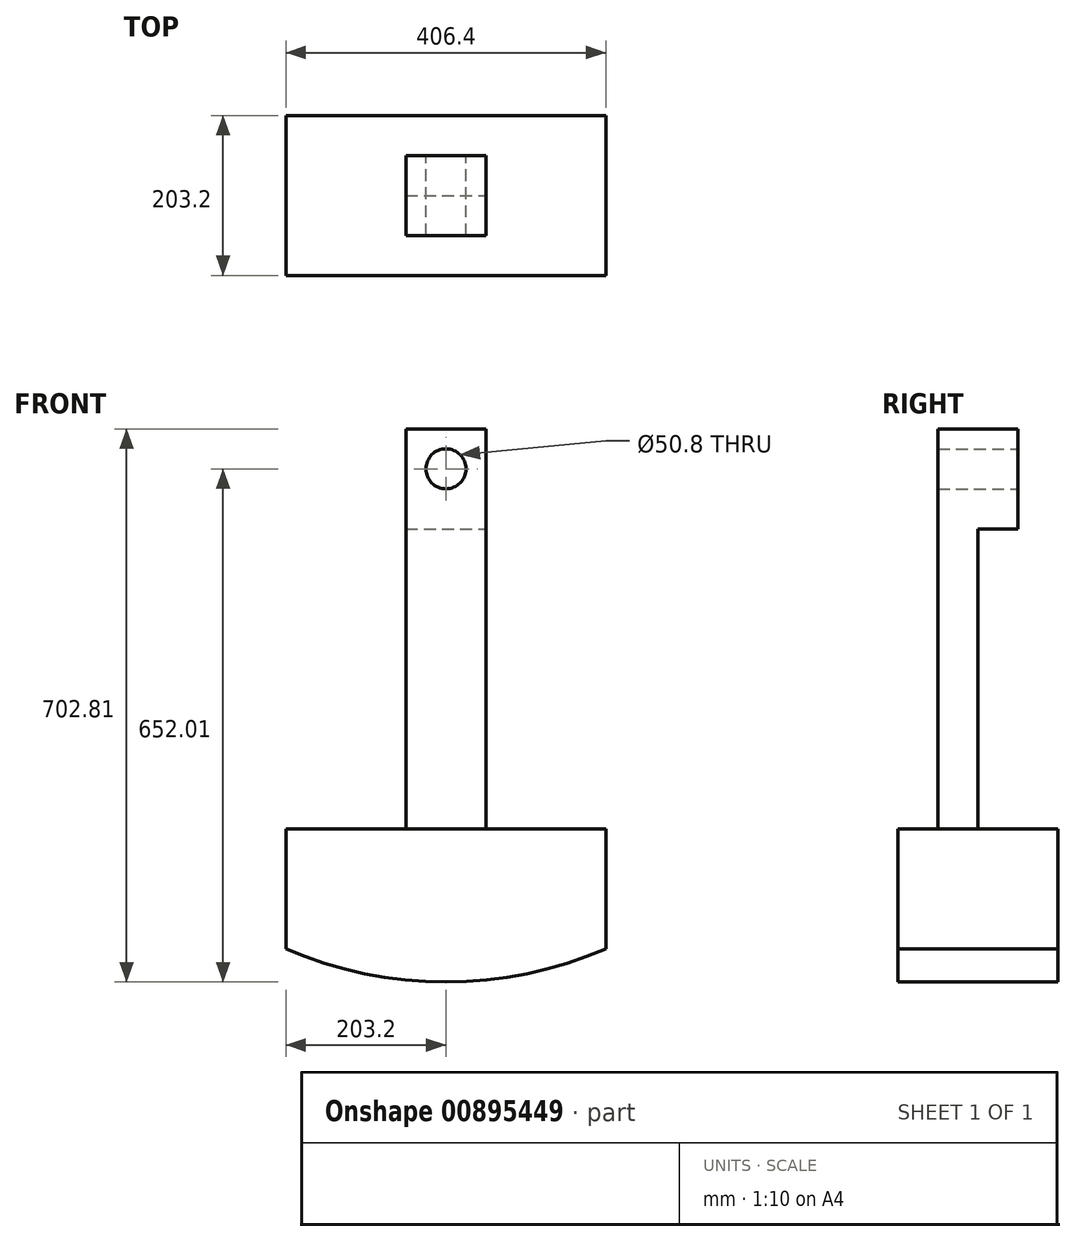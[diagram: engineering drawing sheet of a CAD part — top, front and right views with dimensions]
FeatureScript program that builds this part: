
annotation { "Feature Type Name" : "Feature", "Feature Type Description" : "" }
export const myFeature = defineFeature(function(context is Context, id is Id, definition is map)
    precondition{}
    {
        {
            var Q0;
            Q0=qCreatedBy(makeId("Front.planeOp"),FACE);
            var sketch = newSketch(context, id + "F0", { "sketchPlane" : qUnion([Q0])});
            skLineSegment(sketch, "E0.bottom", {"start": v(-50.8, 0) * mm, "end": v(50.8, 0) * mm});
            skLineSegment(sketch, "E0.top", {"start": v(-50.8, 508) * mm, "end": v(50.8, 508) * mm});
            skLineSegment(sketch, "E0.left", {"start": v(-50.8, 0) * mm, "end": v(-50.8, 508) * mm});
            skLineSegment(sketch, "E0.right", {"start": v(50.8, 0) * mm, "end": v(50.8, 508) * mm});
            skCircle(sketch, "E1", {"center": v(0, 457.2) * mm, "radius": 25.4 * mm});
            skSolve(sketch);
        }
        {
            var Q0;
            Q0=makeQuery(id+"F0.imprint","IMPRINT",FACE,{"disambiguationData":[TD([[makeQuery(id+"F0.imprint","IMPRINT",EDGE,{"derivedFrom":sQuery(id+"F0.wireOp",EDGE,"E0.bottom")}),1.0]])]});
            extrude(context, id + "F1", {"entities" : qUnion([Q0]), "endBound" : BoundingType.SYMMETRIC, "depth" : 101.6 * mm, "offsetDistance" : 25.4 * mm});
        }
        {
            var Q0;
            Q0=qCreatedBy(makeId("Front.planeOp"),FACE);
            var sketch = newSketch(context, id + "F2", { "sketchPlane" : qUnion([Q0])});
            skLineSegment(sketch, "E2", {"start": v(-203.2, 0) * mm, "end": v(203.2, 0) * mm});
            skArc(sketch, "E3", {"start": v(-203.2, -152.4) * mm, "mid": v(0, -194.81) * mm, "end": v(203.2, -152.4) * mm});
            skPoint(sketch, "E3.first.point", {"position": v(0, 821.19) * mm});
            skPoint(sketch, "E3.second.point", {"position": v(0, -194.81) * mm});
            skPoint(sketch, "E3.third.point", {"position": v(254.5, -126.47) * mm});
            skLineSegment(sketch, "E4", {"start": v(-203.2, 0) * mm, "end": v(-203.2, -152.4) * mm});
            skLineSegment(sketch, "E5", {"start": v(203.2, 0) * mm, "end": v(203.2, -152.4) * mm});
            skSolve(sketch);
        }
        {
            var Q0;
            Q0=makeQuery(id+"F2.imprint","IMPRINT",FACE,{"disambiguationData":[TD([[makeQuery(id+"F2.imprint","IMPRINT",EDGE,{"derivedFrom":sQuery(id+"F2.wireOp",EDGE,"E2")}),-1.0]])]});
            extrude(context, id + "F3", {"entities" : qUnion([Q0]), "operationType" : NewBodyOperationType.ADD, "endBound" : BoundingType.SYMMETRIC, "depth" : 203.2 * mm, "offsetDistance" : 25.4 * mm});
        }
        {
            var Q0;
            Q0=makeQuery(id+"F1.opExtrude","SWEPT_FACE",FACE,{"disambiguationData":[OSD([sQuery(id+"F0.wireOp",EDGE,"E0.right")])]});
            var sketch = newSketch(context, id + "F4", { "sketchPlane" : qUnion([Q0])});
            skLineSegment(sketch, "E6.bottom", {"start": v(50.8, 0) * mm, "end": v(0, 0) * mm});
            skLineSegment(sketch, "E6.top", {"start": v(50.8, 381) * mm, "end": v(0, 381) * mm});
            skLineSegment(sketch, "E6.left", {"start": v(50.8, 0) * mm, "end": v(50.8, 381) * mm});
            skLineSegment(sketch, "E6.right", {"start": v(0, 0) * mm, "end": v(0, 381) * mm});
            skSolve(sketch);
        }
        {
            var Q0;
            Q0=makeQuery(id+"F4.imprint","IMPRINT",FACE,{"disambiguationData":[TD([[makeQuery(id+"F4.imprint","IMPRINT",EDGE,{"derivedFrom":sQuery(id+"F4.wireOp",EDGE,"E6.bottom")}),1.0]])]});
            extrude(context, id + "F5", {"entities" : qUnion([Q0]), "operationType" : NewBodyOperationType.REMOVE, "endBound" : BoundingType.THROUGH_ALL, "oppositeDirection" : true, "depth" : 25.4 * mm, "offsetDistance" : 25.4 * mm});
        }
    });
